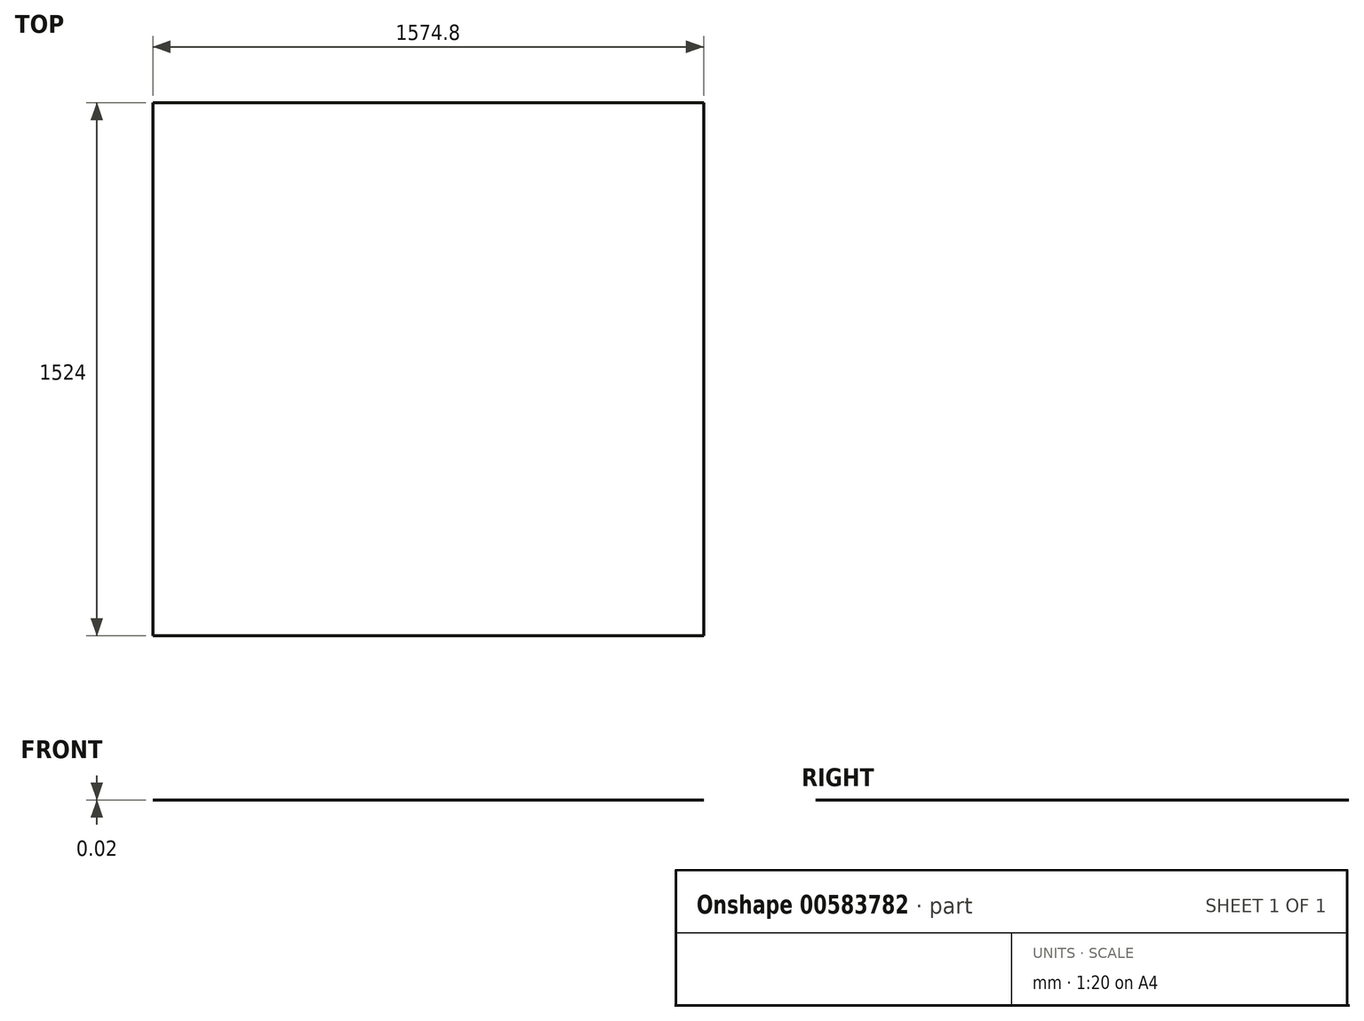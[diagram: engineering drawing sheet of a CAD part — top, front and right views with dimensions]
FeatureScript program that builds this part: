
annotation { "Feature Type Name" : "Feature", "Feature Type Description" : "" }
export const myFeature = defineFeature(function(context is Context, id is Id, definition is map)
    precondition{}
    {
        {
            var Q0;
            Q0=qCreatedBy(makeId("Top.planeOp"),FACE);
            var sketch = newSketch(context, id + "F0", { "sketchPlane" : qUnion([Q0])});
            skLineSegment(sketch, "E0.bottom", {"start": v(779.87, -786.18) * mm, "end": v(-794.93, -786.18) * mm});
            skLineSegment(sketch, "E0.top", {"start": v(779.87, 737.82) * mm, "end": v(-794.93, 737.82) * mm});
            skLineSegment(sketch, "E0.left", {"start": v(779.87, -786.18) * mm, "end": v(779.87, 737.82) * mm});
            skLineSegment(sketch, "E0.right", {"start": v(-794.93, -786.18) * mm, "end": v(-794.93, 737.82) * mm});
            skSolve(sketch);
        }
        {
            var Q0;
            Q0=makeQuery(id+"F0.imprint","IMPRINT",FACE,{"disambiguationData":[TD([[makeQuery(id+"F0.imprint","IMPRINT",EDGE,{"derivedFrom":sQuery(id+"F0.wireOp",EDGE,"E0.bottom")}),-1.0]])]});
            extrude(context, id + "F1", {"entities" : qUnion([Q0]), "depth" : 1 / 50.8 * mm, "offsetDistance" : 25.4 * mm});
        }
    });
